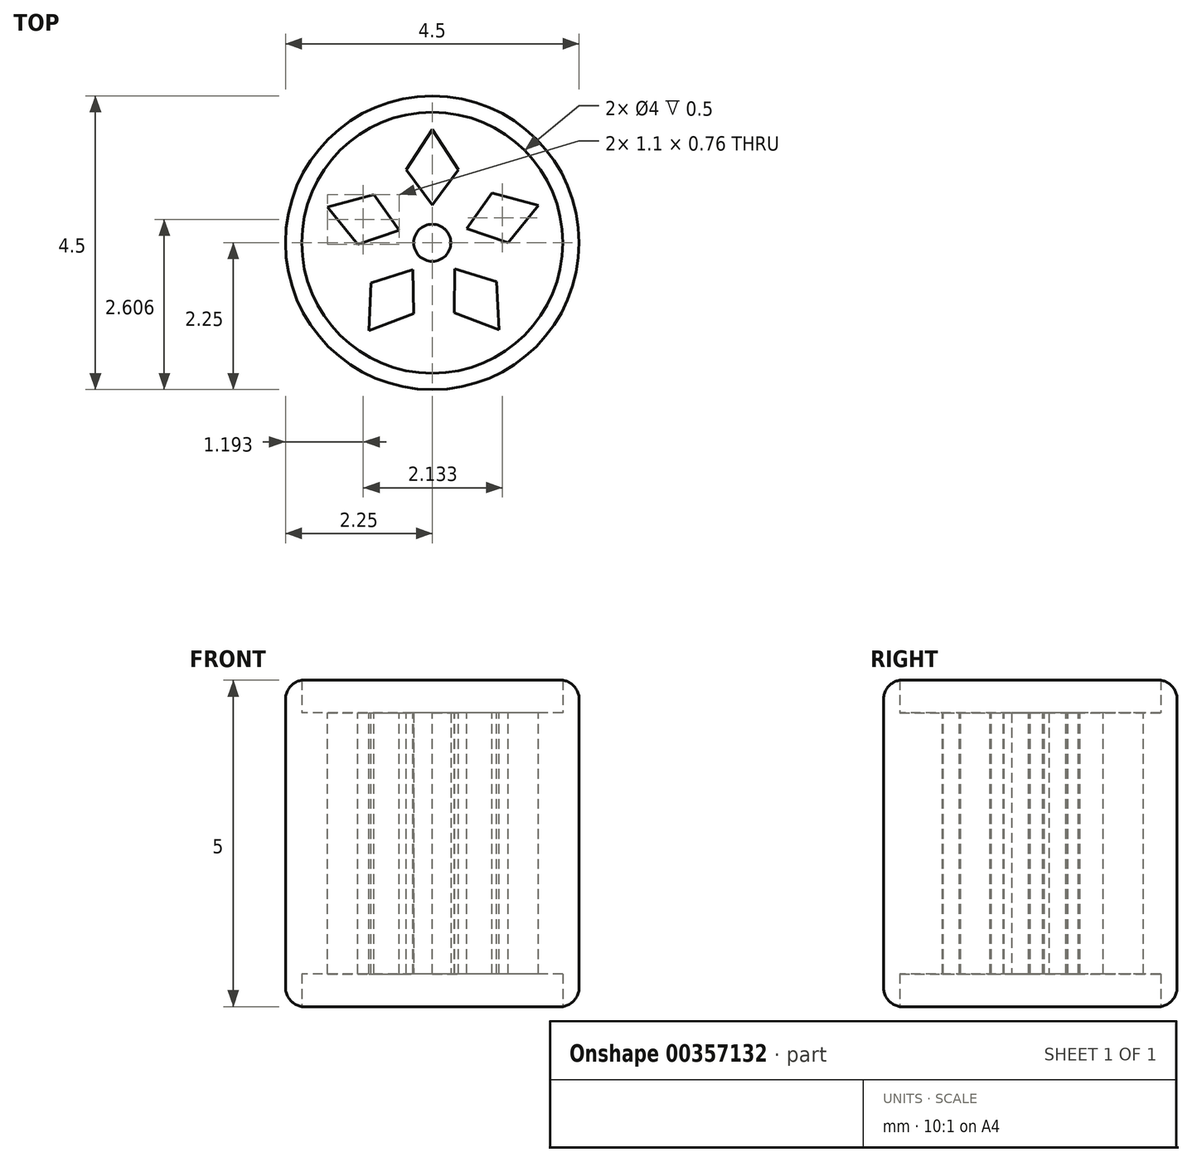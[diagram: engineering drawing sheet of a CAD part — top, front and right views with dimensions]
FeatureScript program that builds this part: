
annotation { "Feature Type Name" : "Feature", "Feature Type Description" : "" }
export const myFeature = defineFeature(function(context is Context, id is Id, definition is map)
    precondition{}
    {
        {
            var Q0;
            Q0=qCreatedBy(makeId("Top.planeOp"),FACE);
            var sketch = newSketch(context, id + "F0", { "sketchPlane" : qUnion([Q0])});
            skCircle(sketch, "E0", {"center": v(0, 0) * mm, "radius": 0.28 * mm});
            skCircle(sketch, "E1", {"center": v(0, 0) * mm, "radius": 2 * mm});
            skCircle(sketch, "E2", {"center": v(0, 0) * mm, "radius": 2.25 * mm});
            skSolve(sketch);
        }
        {
            var Q0;
            Q0=makeQuery(id+"F0.imprint","IMPRINT",FACE,{"disambiguationData":[TD([[makeQuery(id+"F0.imprint","IMPRINT",EDGE,{"derivedFrom":sQuery(id+"F0.wireOp",EDGE,"E0")}),-1.0]])]});
            extrude(context, id + "F1", {"entities" : qUnion([Q0]), "endBound" : BoundingType.SYMMETRIC, "depth" : 4 * mm});
        }
        {
            var Q0;
            Q0 = qSketchRegion(id + "F0", true);
            extrude(context, id + "F2", {"entities" : qUnion([Q0]), "operationType" : NewBodyOperationType.ADD, "endBound" : BoundingType.SYMMETRIC, "depth" : 5 * mm});
        }
        {
            var Q0;
            Q0=qCreatedBy(makeId("Top.planeOp"),FACE);
            var sketch = newSketch(context, id + "F3", { "sketchPlane" : qUnion([Q0])});
            skLineSegment(sketch, "E3", {"start": v(0, 1.73) * mm, "end": v(-0.4, 1.12) * mm});
            skLineSegment(sketch, "E4", {"start": v(-0.4, 1.12) * mm, "end": v(0, 0.58) * mm});
            skLineSegment(sketch, "E5.MirrorCS", {"start": v(0, 1.73) * mm, "end": v(0.4, 1.12) * mm});
            skLineSegment(sketch, "E6.MirrorCS", {"start": v(0.4, 1.12) * mm, "end": v(0, 0.58) * mm});
            skLineSegment(sketch, "E7.1.0", {"start": v(-1.6, 0.55) * mm, "end": v(-0.9, 0.74) * mm});
            skLineSegment(sketch, "E7.1.1", {"start": v(-1.6, 0.55) * mm, "end": v(-1.14, -0.03) * mm});
            skLineSegment(sketch, "E7.1.2", {"start": v(-1.14, -0.03) * mm, "end": v(-0.5, 0.19) * mm});
            skLineSegment(sketch, "E7.1.3", {"start": v(-0.9, 0.74) * mm, "end": v(-0.5, 0.19) * mm});
            skLineSegment(sketch, "E7.2.0", {"start": v(-0.97, -1.35) * mm, "end": v(-0.94, -0.61) * mm});
            skLineSegment(sketch, "E7.2.1", {"start": v(-0.97, -1.35) * mm, "end": v(-0.29, -1.09) * mm});
            skLineSegment(sketch, "E7.2.2", {"start": v(-0.29, -1.09) * mm, "end": v(-0.3, -0.41) * mm});
            skLineSegment(sketch, "E7.2.3", {"start": v(-0.94, -0.61) * mm, "end": v(-0.3, -0.41) * mm});
            skLineSegment(sketch, "E7.3.0", {"start": v(1.02, -1.33) * mm, "end": v(0.34, -1.07) * mm});
            skLineSegment(sketch, "E7.3.1", {"start": v(1.02, -1.33) * mm, "end": v(0.99, -0.6) * mm});
            skLineSegment(sketch, "E7.3.2", {"start": v(0.99, -0.6) * mm, "end": v(0.34, -0.4) * mm});
            skLineSegment(sketch, "E7.3.3", {"start": v(0.34, -1.07) * mm, "end": v(0.34, -0.4) * mm});
            skLineSegment(sketch, "E7.4.0", {"start": v(1.62, 0.57) * mm, "end": v(1.16, 0) * mm});
            skLineSegment(sketch, "E7.4.1", {"start": v(1.62, 0.57) * mm, "end": v(0.92, 0.76) * mm});
            skLineSegment(sketch, "E7.4.2", {"start": v(0.92, 0.76) * mm, "end": v(0.53, 0.21) * mm});
            skLineSegment(sketch, "E7.4.3", {"start": v(1.16, 0) * mm, "end": v(0.53, 0.21) * mm});
            skPoint(sketch, "E7.center", {"position": v(0.01, 0.03) * mm});
            skSolve(sketch);
        }
        {
            var Q0;
            Q0 = qSketchRegion(id + "F3", true);
            extrude(context, id + "F4", {"entities" : qUnion([Q0]), "operationType" : NewBodyOperationType.REMOVE, "endBound" : BoundingType.SYMMETRIC, "oppositeDirection" : true, "depth" : 25 * mm});
        }
        {
            var Q0;
            Q0=makeQuery(id+"F2.opExtrude","SWEPT_FACE",FACE,{"disambiguationData":[OSD([sQuery(id+"F0.wireOp",EDGE,"E2")])]});
            fillet(context, id + "F5", {"entities" : qUnion([Q0]), "radius" : 0.3 * mm, "tangentPropagation" : true, "allowEdgeOverflow" : false});
        }
    });
